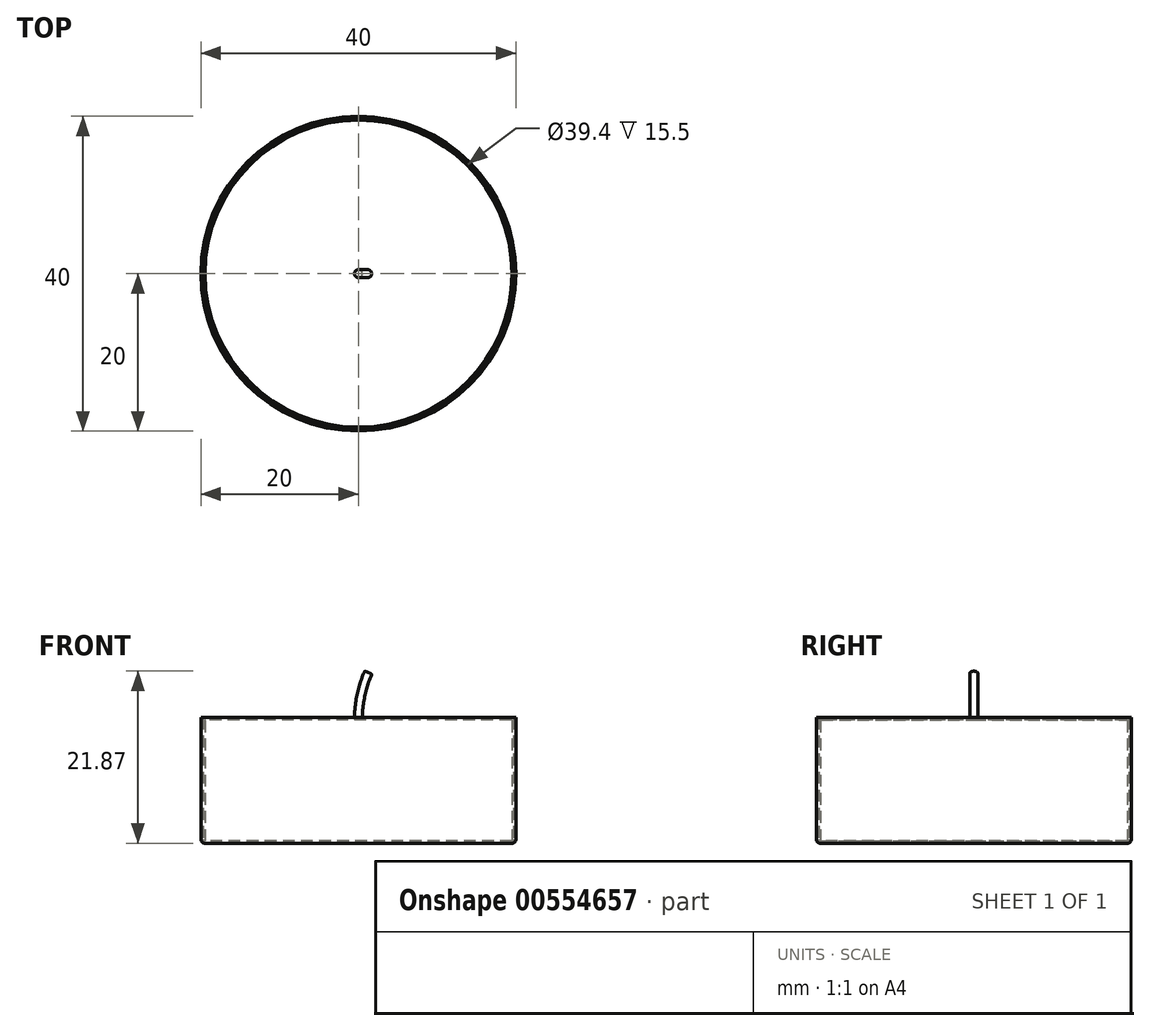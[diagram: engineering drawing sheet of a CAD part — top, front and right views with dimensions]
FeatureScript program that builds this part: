
annotation { "Feature Type Name" : "Feature", "Feature Type Description" : "" }
export const myFeature = defineFeature(function(context is Context, id is Id, definition is map)
    precondition{}
    {
        {
            var Q0;
            Q0=qCreatedBy(makeId("Top.planeOp"),FACE);
            var sketch = newSketch(context, id + "F0", { "sketchPlane" : qUnion([Q0])});
            skCircle(sketch, "E0", {"center": v(0, 0) * mm, "radius": 20 * mm});
            skSolve(sketch);
        }
        {
            var Q0;
            Q0 = qSketchRegion(id + "F0", true);
            extrude(context, id + "F1", {"entities" : qUnion([Q0]), "depth" : 16 * mm, "offsetDistance" : 25 * mm});
        }
        {
            var Q0;
            Q0=makeQuery(id+"F1.opExtrude","CAP_EDGE",EDGE,{"disambiguationData":[OSD([sQuery(id+"F0.wireOp",EDGE,"E0")])],"isStart":true});
            fillet(context, id + "F2", {"entities" : qUnion([Q0]), "radius" : 0.5 * mm, "tangentPropagation" : true, "allowEdgeOverflow" : false});
        }
        {
            var Q0;
            Q0=makeQuery(id+"F1.opExtrude","CAP_FACE",FACE,{"disambiguationData":[OSD([sQuery(id+"F0.wireOp",EDGE,"E0")])],"isStart":false});
            shell(context, id + "F3", {"entities" : qUnion([Q0]), "thickness" : 0.3 * mm});
        }
        {
            var Q0;
            Q0=qCreatedBy(makeId("Top.planeOp"),FACE);
            var sketch = newSketch(context, id + "F4", { "sketchPlane" : qUnion([Q0])});
            skCircle(sketch, "E1", {"center": v(0, 0) * mm, "radius": 19.5 * mm});
            skSolve(sketch);
        }
        {
            var Q0;
            Q0 = qSketchRegion(id + "F4", true);
            extrude(context, id + "F5", {"entities" : qUnion([Q0]), "depth" : 15.7 * mm, "offsetDistance" : 25 * mm});
        }
        {
            var Q0;
            Q0=qCreatedBy(makeId("Front.planeOp"),FACE);
            var sketch = newSketch(context, id + "F6", { "sketchPlane" : qUnion([Q0])});
            skLineSegment(sketch, "E2", {"start": v(0, 0) * mm, "end": v(0, 15.7) * mm, "construction": true});
            skArc(sketch, "E3", {"start": v(1.25, 21.7) * mm, "mid": v(0.32, 18.76) * mm, "end": v(0, 15.7) * mm});
            skSolve(sketch);
        }
        {
            var Q0;
            Q0=makeQuery(id+"F5.opExtrude","CAP_FACE",FACE,{"disambiguationData":[OSD([sQuery(id+"F4.wireOp",EDGE,"E1")])],"isStart":false});
            var sketch = newSketch(context, id + "F7", { "sketchPlane" : qUnion([Q0])});
            skCircle(sketch, "E4", {"center": v(0, 0) * mm, "radius": 0.5 * mm});
            skSolve(sketch);
        }
        {
            var Q0;
            Q0=makeQuery(id+"F7.imprint","IMPRINT",FACE,{"disambiguationData":[TD([[makeQuery(id+"F7.imprint","IMPRINT",EDGE,{"derivedFrom":sQuery(id+"F7.wireOp",EDGE,"E4")}),1.0]])]});
            var Q1;
            Q1=sQuery(id+"F6.wireOp",EDGE,"E3");
            sweep(context, id + "F8", {"profiles" : qUnion([Q0]), "path" : qUnion([Q1])});
        }
        {
            var Q0;
            Q0=makeQuery(id+"F8.opSweep","CAP_EDGE",EDGE,{"disambiguationData":[OSD([sQuery(id+"F6.wireOp",VERTEX,"E3.start"),sQuery(id+"F7.wireOp",EDGE,"E4")])],"isStart":false});
            fillet(context, id + "F9", {"entities" : qUnion([Q0]), "radius" : 0.1 * mm, "tangentPropagation" : true, "allowEdgeOverflow" : false});
        }
        {
            var Q0;
            Q0=makeQuery(id+"F5.opExtrude","CAP_EDGE",EDGE,{"disambiguationData":[OSD([sQuery(id+"F4.wireOp",EDGE,"E1")])],"isStart":false});
            fillet(context, id + "F10", {"entities" : qUnion([Q0]), "radius" : 0.1 * mm, "tangentPropagation" : true, "allowEdgeOverflow" : false});
        }
    });
